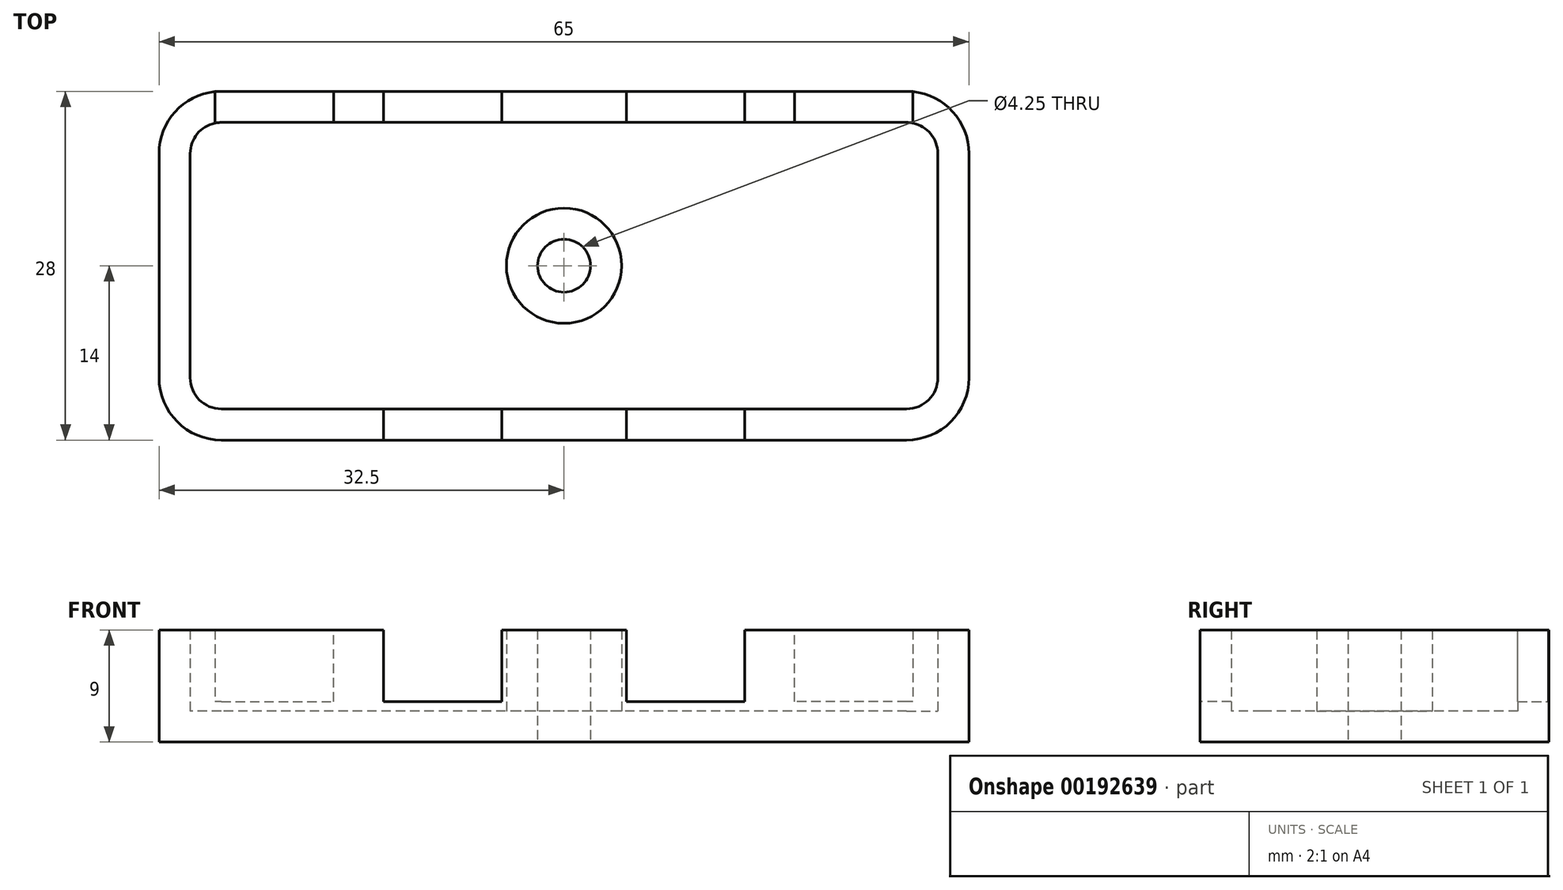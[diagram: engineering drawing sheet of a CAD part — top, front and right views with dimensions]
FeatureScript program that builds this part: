
annotation { "Feature Type Name" : "Feature", "Feature Type Description" : "" }
export const myFeature = defineFeature(function(context is Context, id is Id, definition is map)
    precondition{}
    {
        {
            var Q0;
            Q0=qCreatedBy(makeId("Top.planeOp"),FACE);
            var sketch = newSketch(context, id + "F0", { "sketchPlane" : qUnion([Q0])});
            skLineSegment(sketch, "E0.bottom", {"start": v(27.5, 14) * mm, "end": v(-27.5, 14) * mm});
            skLineSegment(sketch, "E0.top", {"start": v(27.5, -14) * mm, "end": v(-27.5, -14) * mm});
            skLineSegment(sketch, "E0.left", {"start": v(32.5, 9) * mm, "end": v(32.5, -9) * mm});
            skLineSegment(sketch, "E0.right", {"start": v(-32.5, 9) * mm, "end": v(-32.5, -9) * mm});
            skPoint(sketch, "E0.middle", {"position": v(0, 0) * mm});
            skPoint(sketch, "E1.visualSharp", {"position": v(-32.5, 14) * mm});
            skArc(sketch, "E1.filletArc", {"start": v(-27.5, 14) * mm, "mid": v(-31.04, 12.54) * mm, "end": v(-32.5, 9) * mm});
            skPoint(sketch, "E2.visualSharp", {"position": v(-32.5, -14) * mm});
            skArc(sketch, "E2.filletArc", {"start": v(-32.5, -9) * mm, "mid": v(-31.04, -12.54) * mm, "end": v(-27.5, -14) * mm});
            skPoint(sketch, "E3.visualSharp", {"position": v(32.5, -14) * mm});
            skArc(sketch, "E3.filletArc", {"start": v(27.5, -14) * mm, "mid": v(31.04, -12.54) * mm, "end": v(32.5, -9) * mm});
            skPoint(sketch, "E4.visualSharp", {"position": v(32.5, 14) * mm});
            skArc(sketch, "E4.filletArc", {"start": v(32.5, 9) * mm, "mid": v(31.04, 12.54) * mm, "end": v(27.5, 14) * mm});
            skCircle(sketch, "E5", {"center": v(0, 0) * mm, "radius": 2.12 * mm});
            skSolve(sketch);
        }
        {
            var Q0;
            Q0=makeQuery(id+"F0.imprint","IMPRINT",FACE,{"disambiguationData":[TD([[makeQuery(id+"F0.imprint","IMPRINT",EDGE,{"derivedFrom":sQuery(id+"F0.wireOp",EDGE,"E0.bottom")}),1.0]])]});
            extrude(context, id + "F1", {"entities" : qUnion([Q0]), "depth" : 9 * mm});
        }
        {
            var Q0;
            Q0=makeQuery(id+"F1.opExtrude","CAP_FACE",FACE,{"disambiguationData":[OSD([sQuery(id+"F0.wireOp",EDGE,"E0.bottom"),sQuery(id+"F0.wireOp",EDGE,"E0.top"),sQuery(id+"F0.wireOp",EDGE,"E0.left"),sQuery(id+"F0.wireOp",EDGE,"E0.right")])],"isStart":false});
            shell(context, id + "F2", {"entities" : qUnion([Q0]), "thickness" : 2.5 * mm});
        }
        {
            var Q0;
            Q0=makeQuery(id+"F1.opExtrude","CAP_FACE",FACE,{"disambiguationData":[OSD([sQuery(id+"F0.wireOp",EDGE,"E0.bottom"),sQuery(id+"F0.wireOp",EDGE,"E0.top"),sQuery(id+"F0.wireOp",EDGE,"E0.left"),sQuery(id+"F0.wireOp",EDGE,"E0.right"),sQuery(id+"F0.wireOp",EDGE,"E1.filletArc"),sQuery(id+"F0.wireOp",EDGE,"E2.filletArc"),sQuery(id+"F0.wireOp",EDGE,"E3.filletArc"),sQuery(id+"F0.wireOp",EDGE,"E4.filletArc"),sQuery(id+"F0.wireOp",EDGE,"E5")])],"isStart":false});
            var sketch = newSketch(context, id + "F3", { "sketchPlane" : qUnion([Q0])});
            skLineSegment(sketch, "E6.bottom", {"start": v(5, 0) * mm, "end": v(14.5, 0) * mm});
            skLineSegment(sketch, "E6.top", {"start": v(5, -14) * mm, "end": v(14.5, -14) * mm});
            skLineSegment(sketch, "E6.left", {"start": v(5, 0) * mm, "end": v(5, -14) * mm});
            skLineSegment(sketch, "E6.right", {"start": v(14.5, 0) * mm, "end": v(14.5, -14) * mm});
            skLineSegment(sketch, "E7", {"start": v(16.5, 0) * mm, "end": v(16.5, -22.85) * mm, "construction": true});
            skPoint(sketch, "E7.startSnap0", {"position": v(9.75, 0) * mm});
            skLineSegment(sketch, "E8.MirrorCS", {"start": v(-5, 0) * mm, "end": v(-14.5, 0) * mm});
            skLineSegment(sketch, "E9.MirrorCS", {"start": v(-5, -14) * mm, "end": v(-14.5, -14) * mm});
            skLineSegment(sketch, "E10.MirrorCS", {"start": v(-5, 0) * mm, "end": v(-5, -14) * mm});
            skLineSegment(sketch, "E11.MirrorCS", {"start": v(-14.5, 0) * mm, "end": v(-14.5, -14) * mm});
            skPoint(sketch, "E12.MirrorP", {"position": v(-9.75, 0) * mm});
            skLineSegment(sketch, "E13.MirrorCS", {"start": v(-14.5, 0) * mm, "end": v(-14.5, 14) * mm});
            skLineSegment(sketch, "E14.MirrorCS", {"start": v(-5, 0) * mm, "end": v(-5, 14) * mm});
            skLineSegment(sketch, "E15.MirrorCS", {"start": v(-5, 14) * mm, "end": v(-14.5, 14) * mm});
            skLineSegment(sketch, "E16.MirrorCS", {"start": v(16.5, 0) * mm, "end": v(16.5, 22.85) * mm, "construction": true});
            skLineSegment(sketch, "E17.MirrorCS", {"start": v(14.5, 0) * mm, "end": v(14.5, 14) * mm});
            skLineSegment(sketch, "E18.MirrorCS", {"start": v(5, 0) * mm, "end": v(5, 14) * mm});
            skLineSegment(sketch, "E19.MirrorCS", {"start": v(5, 14) * mm, "end": v(14.5, 14) * mm});
            skPoint(sketch, "E20.MirrorP", {"position": v(23.25, 0) * mm});
            skLineSegment(sketch, "E21.MirrorCS", {"start": v(28, 0) * mm, "end": v(18.5, 0) * mm});
            skLineSegment(sketch, "E22.MirrorCS", {"start": v(28, 14) * mm, "end": v(18.5, 14) * mm});
            skLineSegment(sketch, "E23.MirrorCS", {"start": v(28, 0) * mm, "end": v(28, 14) * mm});
            skLineSegment(sketch, "E24.MirrorCS", {"start": v(18.5, 0) * mm, "end": v(18.5, 14) * mm});
            skPoint(sketch, "E25.MirrorP", {"position": v(-23.25, 0) * mm});
            skLineSegment(sketch, "E26.MirrorCS", {"start": v(-28, 0) * mm, "end": v(-18.5, 0) * mm});
            skLineSegment(sketch, "E27.MirrorCS", {"start": v(-28, 0) * mm, "end": v(-28, 14) * mm});
            skLineSegment(sketch, "E28.MirrorCS", {"start": v(-28, 14) * mm, "end": v(-18.5, 14) * mm});
            skLineSegment(sketch, "E29.MirrorCS", {"start": v(-18.5, 0) * mm, "end": v(-18.5, 14) * mm});
            skSolve(sketch);
        }
        {
            var Q0;
            Q0 = qSketchRegion(id + "F3", true);
            extrude(context, id + "F4", {"entities" : qUnion([Q0]), "operationType" : NewBodyOperationType.REMOVE, "oppositeDirection" : true, "depth" : 5.75 * mm});
        }
    });
